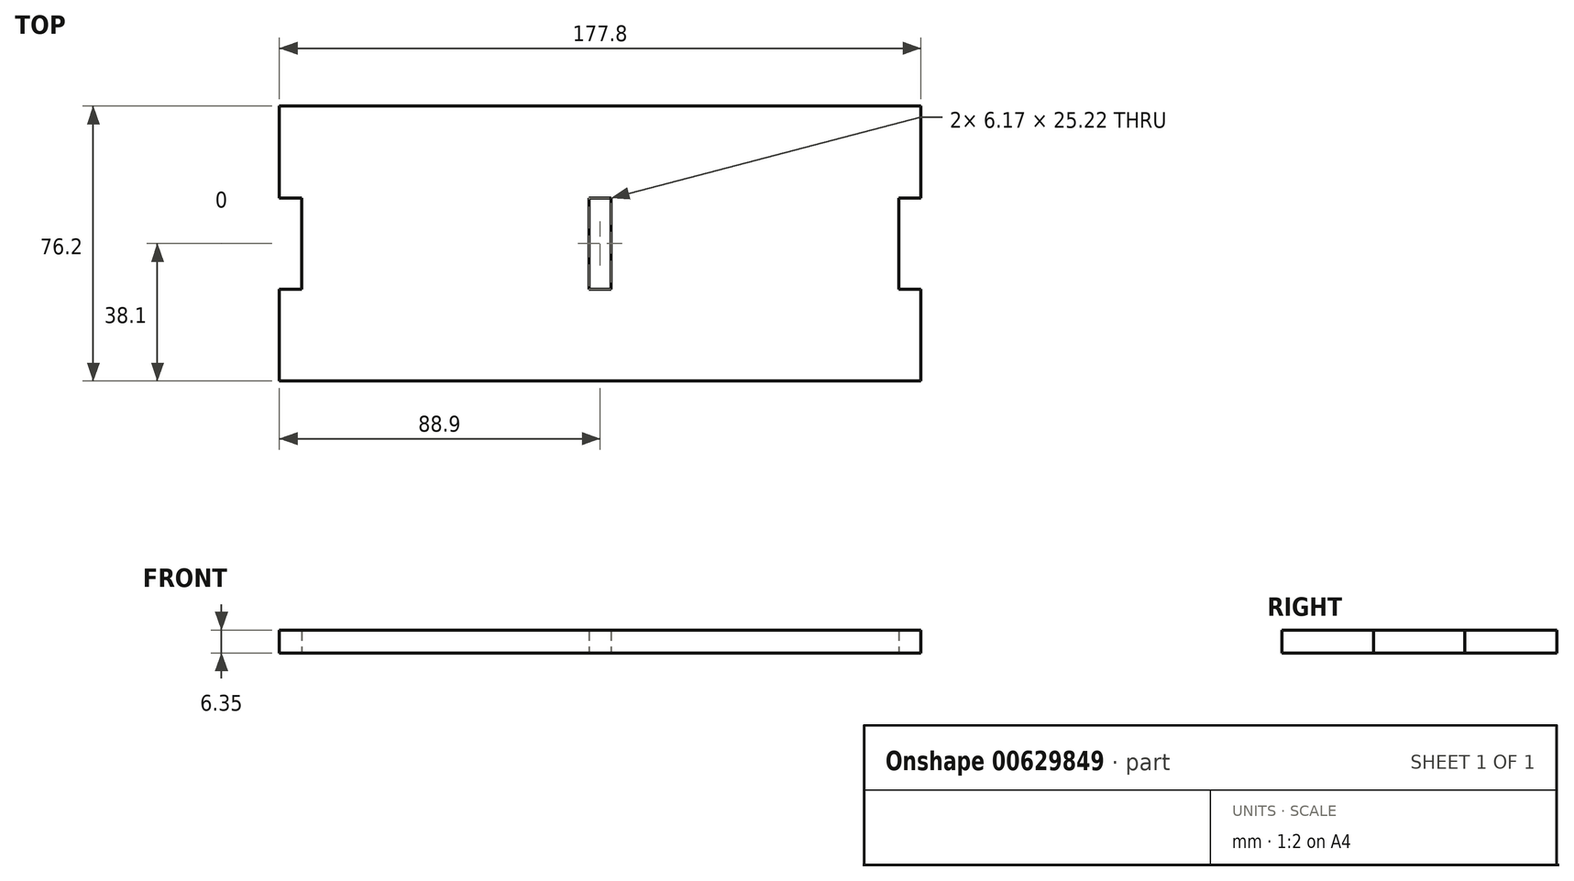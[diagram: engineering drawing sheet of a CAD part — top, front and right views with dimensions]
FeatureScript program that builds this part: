
annotation { "Feature Type Name" : "Feature", "Feature Type Description" : "" }
export const myFeature = defineFeature(function(context is Context, id is Id, definition is map)
    precondition{}
    {
        {
            var Q0;
            Q0=qCreatedBy(makeId("Top.planeOp"),FACE);
            var sketch = newSketch(context, id + "F0", { "sketchPlane" : qUnion([Q0])});
            skLineSegment(sketch, "E0.bottom", {"start": v(0, 0) * mm, "end": v(177.8, 0) * mm});
            skLineSegment(sketch, "E0.top", {"start": v(0, 76.2) * mm, "end": v(177.8, 76.2) * mm});
            skLineSegment(sketch, "E0.left", {"start": v(0, 0) * mm, "end": v(0, 76.2) * mm});
            skLineSegment(sketch, "E0.right", {"start": v(177.8, 0) * mm, "end": v(177.8, 76.2) * mm});
            skLineSegment(sketch, "E1.bottom", {"start": v(25.31, 0) * mm, "end": v(50.89, 0) * mm});
            skLineSegment(sketch, "E1.top", {"start": v(25.31, -6.44) * mm, "end": v(50.89, -6.44) * mm});
            skLineSegment(sketch, "E1.left", {"start": v(25.31, 0) * mm, "end": v(25.31, -6.44) * mm});
            skLineSegment(sketch, "E1.right", {"start": v(50.89, 0) * mm, "end": v(50.89, -6.44) * mm});
            skLineSegment(sketch, "E2.bottom", {"start": v(76.11, 0) * mm, "end": v(101.69, 0) * mm});
            skLineSegment(sketch, "E2.top", {"start": v(76.11, -6.44) * mm, "end": v(101.69, -6.44) * mm});
            skLineSegment(sketch, "E2.left", {"start": v(76.11, 0) * mm, "end": v(76.11, -6.44) * mm});
            skLineSegment(sketch, "E2.right", {"start": v(101.69, 0) * mm, "end": v(101.69, -6.44) * mm});
            skLineSegment(sketch, "E3.bottom", {"start": v(126.91, 0) * mm, "end": v(152.49, 0) * mm});
            skLineSegment(sketch, "E3.top", {"start": v(126.91, -6.44) * mm, "end": v(152.49, -6.44) * mm});
            skLineSegment(sketch, "E3.left", {"start": v(126.91, 0) * mm, "end": v(126.91, -6.44) * mm});
            skLineSegment(sketch, "E3.right", {"start": v(152.49, 0) * mm, "end": v(152.49, -6.44) * mm});
            skPoint(sketch, "E4", {"position": v(38.1, 0) * mm});
            skPoint(sketch, "E5", {"position": v(88.9, 0) * mm});
            skPoint(sketch, "E6", {"position": v(139.7, 0) * mm});
            skLineSegment(sketch, "E7.bottom", {"start": v(0, 50.71) * mm, "end": v(6.17, 50.71) * mm});
            skLineSegment(sketch, "E7.top", {"start": v(0, 25.49) * mm, "end": v(6.17, 25.49) * mm});
            skLineSegment(sketch, "E7.left", {"start": v(0, 50.71) * mm, "end": v(0, 25.49) * mm});
            skLineSegment(sketch, "E7.right", {"start": v(6.17, 50.71) * mm, "end": v(6.17, 25.49) * mm});
            skLineSegment(sketch, "E8.bottom", {"start": v(171.63, 50.71) * mm, "end": v(177.8, 50.71) * mm});
            skLineSegment(sketch, "E8.top", {"start": v(171.63, 25.49) * mm, "end": v(177.8, 25.49) * mm});
            skLineSegment(sketch, "E8.left", {"start": v(171.63, 50.71) * mm, "end": v(171.63, 25.49) * mm});
            skLineSegment(sketch, "E8.right", {"start": v(177.8, 50.71) * mm, "end": v(177.8, 25.49) * mm});
            skPoint(sketch, "E9", {"position": v(177.8, 38.1) * mm});
            skPoint(sketch, "E10", {"position": v(0, 38.1) * mm});
            skPoint(sketch, "E11", {"position": v(6.17, 38.1) * mm});
            skLineSegment(sketch, "E12.bottom", {"start": v(85.81, 50.71) * mm, "end": v(91.99, 50.71) * mm});
            skLineSegment(sketch, "E12.top", {"start": v(85.81, 25.49) * mm, "end": v(91.99, 25.49) * mm});
            skLineSegment(sketch, "E12.left", {"start": v(85.81, 50.71) * mm, "end": v(85.81, 25.49) * mm});
            skLineSegment(sketch, "E12.right", {"start": v(91.99, 50.71) * mm, "end": v(91.99, 25.49) * mm});
            skPoint(sketch, "E13", {"position": v(85.81, 38.1) * mm});
            skPoint(sketch, "E14", {"position": v(88.9, 25.49) * mm});
            skSolve(sketch);
        }
        {
            var Q0;
            {var subQ2=sQuery(id+"F0.wireOp",EDGE,"E0.top");Q0=makeQuery(id+"F0.imprint","IMPRINT",FACE,{"disambiguationData":[TD([[makeQuery(id+"F0.imprint","IMPRINT",EDGE,{"derivedFrom":subQ2}),-1.0]])]});}
            var Q1;
            Q1=makeQuery(id+"F0.imprint","IMPRINT",FACE,{"disambiguationData":[TD([[makeQuery(id+"F0.imprint","IMPRINT",EDGE,{"derivedFrom":sQuery(id+"F0.wireOp",EDGE,"E1.bottom")}),-1.0]])]});
            var Q2;
            Q2=makeQuery(id+"F0.imprint","IMPRINT",FACE,{"disambiguationData":[TD([[makeQuery(id+"F0.imprint","IMPRINT",EDGE,{"derivedFrom":sQuery(id+"F0.wireOp",EDGE,"E2.bottom")}),-1.0]])]});
            var Q3;
            Q3=makeQuery(id+"F0.imprint","IMPRINT",FACE,{"disambiguationData":[TD([[makeQuery(id+"F0.imprint","IMPRINT",EDGE,{"derivedFrom":sQuery(id+"F0.wireOp",EDGE,"E3.bottom")}),-1.0]])]});
            extrude(context, id + "F1", {"entities" : qUnion([Q0, Q1, Q2, Q3]), "depth" : 6.35 * mm, "offsetDistance" : 25.4 * mm});
        }
    });
